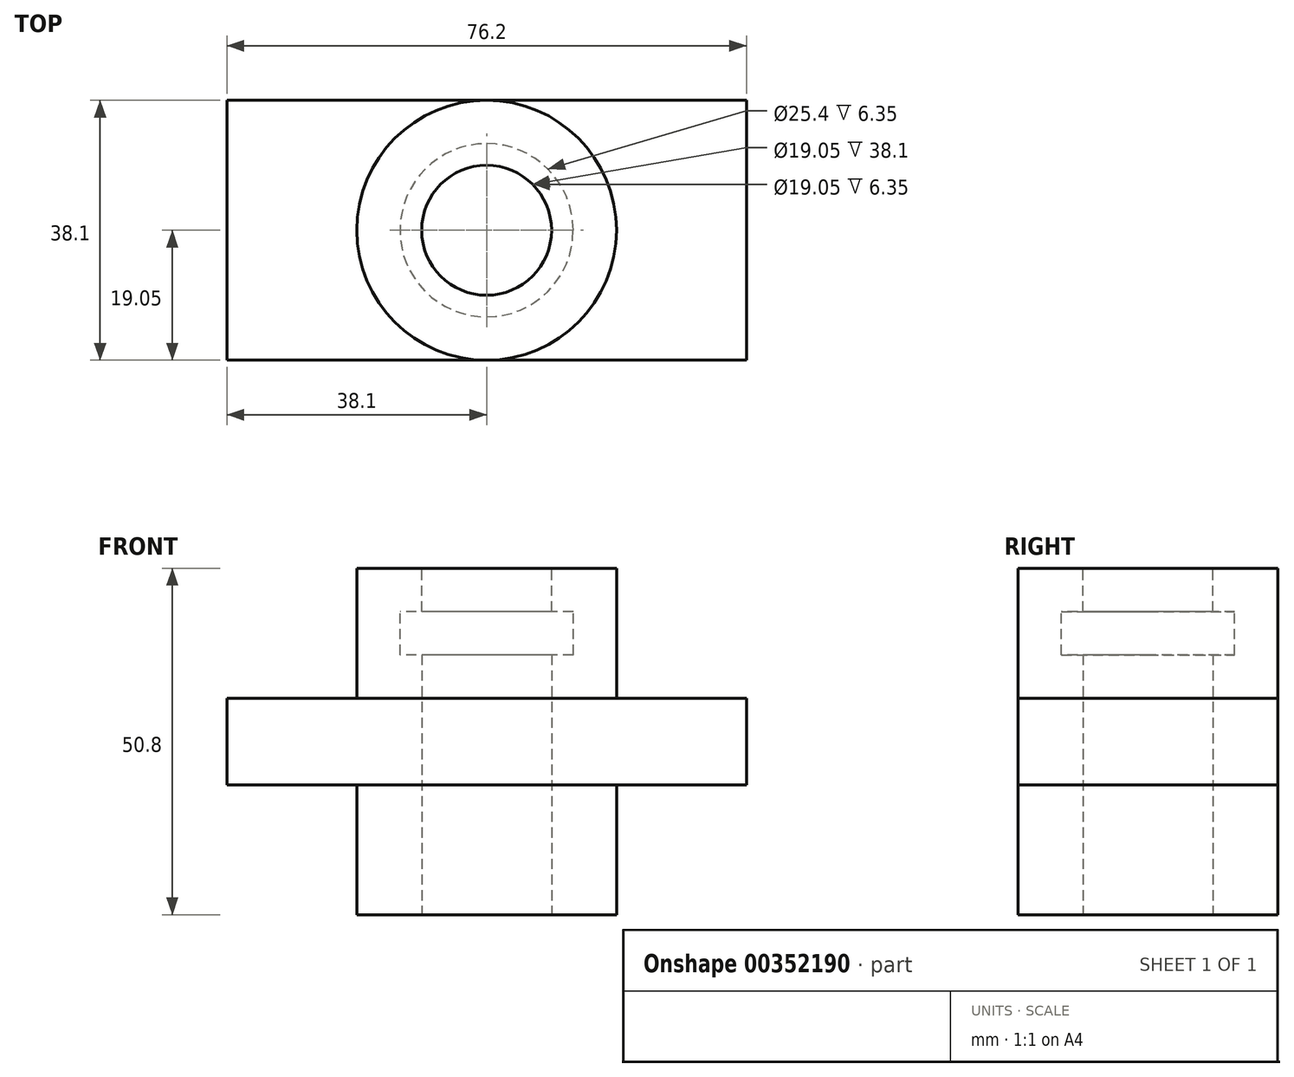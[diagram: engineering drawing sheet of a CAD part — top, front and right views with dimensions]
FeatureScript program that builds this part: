
annotation { "Feature Type Name" : "Feature", "Feature Type Description" : "" }
export const myFeature = defineFeature(function(context is Context, id is Id, definition is map)
    precondition{}
    {
        {
            var Q0;
            Q0=qCreatedBy(makeId("Top.planeOp"),FACE);
            var sketch = newSketch(context, id + "F0", { "sketchPlane" : qUnion([Q0])});
            skLineSegment(sketch, "E0.bottom", {"start": v(0, 0) * mm, "end": v(-76.2, 0) * mm});
            skLineSegment(sketch, "E0.top", {"start": v(0, -38.1) * mm, "end": v(-76.2, -38.1) * mm});
            skLineSegment(sketch, "E0.left", {"start": v(0, 0) * mm, "end": v(0, -38.1) * mm});
            skLineSegment(sketch, "E0.right", {"start": v(-76.2, 0) * mm, "end": v(-76.2, -38.1) * mm});
            skSolve(sketch);
        }
        {
            var Q0;
            Q0=makeQuery(id+"F0.imprint","IMPRINT",FACE,{"disambiguationData":[TD([[makeQuery(id+"F0.imprint","IMPRINT",EDGE,{"derivedFrom":sQuery(id+"F0.wireOp",EDGE,"E0.bottom")}),1.0]])]});
            extrude(context, id + "F1", {"entities" : qUnion([Q0]), "depth" : 12.7 * mm});
        }
        {
            var Q0;
            Q0=makeQuery(id+"F1.opExtrude","CAP_FACE",FACE,{"disambiguationData":[OSD([sQuery(id+"F0.wireOp",EDGE,"E0.bottom"),sQuery(id+"F0.wireOp",EDGE,"E0.top"),sQuery(id+"F0.wireOp",EDGE,"E0.left"),sQuery(id+"F0.wireOp",EDGE,"E0.right")])],"isStart":false});
            var sketch = newSketch(context, id + "F2", { "sketchPlane" : qUnion([Q0])});
            skCircle(sketch, "E1", {"center": v(-38.1, -19.05) * mm, "radius": 19.05 * mm});
            skPoint(sketch, "E1.centerSnap0", {"position": v(-38.1, 0) * mm});
            skPoint(sketch, "E1.centerSnap1", {"position": v(0, -19.05) * mm});
            skCircle(sketch, "E2", {"center": v(-38.1, -19.05) * mm, "radius": 9.53 * mm});
            skSolve(sketch);
        }
        {
            var Q0;
            Q0=makeQuery(id+"F2.imprint","IMPRINT",FACE,{"disambiguationData":[TD([[makeQuery(id+"F2.imprint","IMPRINT",EDGE,{"derivedFrom":sQuery(id+"F2.wireOp",EDGE,"E2")}),-1.0]])]});
            extrude(context, id + "F3", {"entities" : qUnion([Q0]), "operationType" : NewBodyOperationType.ADD, "depth" : 19.05 * mm});
        }
        {
            var Q0;
            Q0=makeQuery(id+"F1.opExtrude","CAP_FACE",FACE,{"disambiguationData":[OSD([sQuery(id+"F0.wireOp",EDGE,"E0.bottom"),sQuery(id+"F0.wireOp",EDGE,"E0.top"),sQuery(id+"F0.wireOp",EDGE,"E0.left"),sQuery(id+"F0.wireOp",EDGE,"E0.right")])],"isStart":true});
            var sketch = newSketch(context, id + "F4", { "sketchPlane" : qUnion([Q0])});
            skCircle(sketch, "E3", {"center": v(-38.1, 19.05) * mm, "radius": 19.05 * mm});
            skPoint(sketch, "E3.centerSnap0", {"position": v(0, 19.05) * mm});
            skPoint(sketch, "E3.centerSnap1", {"position": v(-38.1, 38.1) * mm});
            skCircle(sketch, "E4", {"center": v(-38.1, 19.05) * mm, "radius": 9.53 * mm});
            skSolve(sketch);
        }
        {
            var Q0;
            Q0=makeQuery(id+"F4.imprint","IMPRINT",FACE,{"disambiguationData":[TD([[makeQuery(id+"F4.imprint","IMPRINT",EDGE,{"derivedFrom":sQuery(id+"F4.wireOp",EDGE,"E4")}),-1.0]])]});
            extrude(context, id + "F5", {"entities" : qUnion([Q0]), "operationType" : NewBodyOperationType.ADD, "depth" : 19.05 * mm});
        }
        {
            var Q0;
            Q0=makeQuery(id+"F3.boolean.opBoolean","SPLIT",FACE,{"disambiguationData":[TD([makeQuery(id+"F3.opExtrude","SWEPT_FACE",FACE,{"disambiguationData":[OSD([sQuery(id+"F2.wireOp",EDGE,"E2")])]})])],"derivedFrom":makeQuery(id+"F1.opExtrude","CAP_FACE",FACE,{"disambiguationData":[OSD([sQuery(id+"F0.wireOp",EDGE,"E0.bottom"),sQuery(id+"F0.wireOp",EDGE,"E0.top"),sQuery(id+"F0.wireOp",EDGE,"E0.left"),sQuery(id+"F0.wireOp",EDGE,"E0.right")])],"isStart":false})});
            extrude(context, id + "F6", {"entities" : qUnion([Q0]), "operationType" : NewBodyOperationType.REMOVE, "endBound" : BoundingType.THROUGH_ALL, "oppositeDirection" : true, "depth" : 25.4 * mm});
        }
        {
            var Q0;
            Q0=makeQuery(id+"F3.opExtrude","CAP_FACE",FACE,{"disambiguationData":[OSD([sQuery(id+"F2.wireOp",EDGE,"E1"),sQuery(id+"F2.wireOp",EDGE,"E2")])],"isStart":false});
            var sketch = newSketch(context, id + "F7", { "sketchPlane" : qUnion([Q0])});
            skCircle(sketch, "E5", {"center": v(-38.1, -19.05) * mm, "radius": 12.7 * mm});
            skSolve(sketch);
        }
        {
            var Q0;
            Q0=makeQuery(id+"F7.imprint","IMPRINT",FACE,{"disambiguationData":[TD([[makeQuery(id+"F7.imprint","IMPRINT",EDGE,{"derivedFrom":sQuery(id+"F7.wireOp",EDGE,"E5")}),1.0]])]});
            extrude(context, id + "F8", {"entities" : qUnion([Q0]), "operationType" : NewBodyOperationType.REMOVE, "oppositeDirection" : true, "depth" : 12.7 * mm, "hasSecondDirection" : true, "secondDirectionOppositeDirection" : false, "secondDirectionDepth" : 25.4 * mm});
        }
        {
            var Q0;
            Q0=makeQuery(id+"F3.opExtrude","CAP_FACE",FACE,{"disambiguationData":[OSD([sQuery(id+"F2.wireOp",EDGE,"E1"),sQuery(id+"F2.wireOp",EDGE,"E2")])],"isStart":false});
            var sketch = newSketch(context, id + "F9", { "sketchPlane" : qUnion([Q0])});
            skCircle(sketch, "E6", {"center": v(-38.1, -19.05) * mm, "radius": 9.53 * mm});
            skSolve(sketch);
        }
        {
            var Q0;
            Q0=makeQuery(id+"F9.imprint","IMPRINT",FACE,{"disambiguationData":[TD([[makeQuery(id+"F9.imprint","IMPRINT",EDGE,{"derivedFrom":sQuery(id+"F9.wireOp",EDGE,"E6")}),-1.0]])]});
            extrude(context, id + "F10", {"entities" : qUnion([Q0]), "operationType" : NewBodyOperationType.ADD, "oppositeDirection" : true, "depth" : 6.35 * mm});
        }
    });
